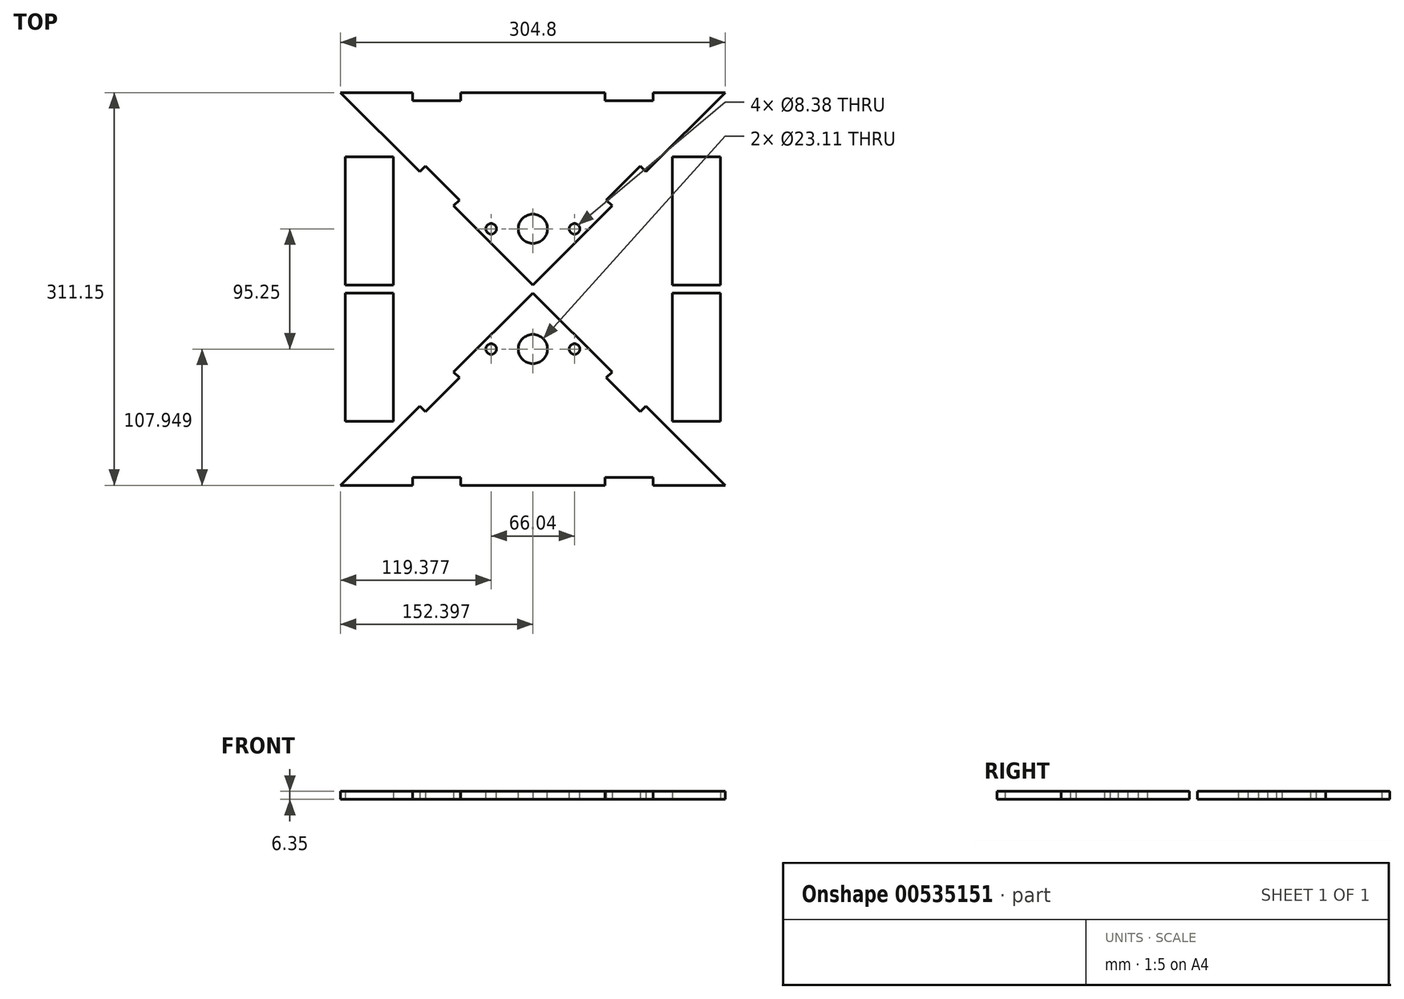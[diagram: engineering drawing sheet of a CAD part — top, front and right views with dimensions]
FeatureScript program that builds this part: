
annotation { "Feature Type Name" : "Feature", "Feature Type Description" : "" }
export const myFeature = defineFeature(function(context is Context, id is Id, definition is map)
    precondition{}
    {
        {
            var Q0;
            Q0=qCreatedBy(makeId("Top.planeOp"),FACE);
            var sketch = newSketch(context, id + "F0", { "sketchPlane" : qUnion([Q0])});
            skLineSegment(sketch, "E0", {"start": v(-161.55, -33.56) * mm, "end": v(143.25, -33.56) * mm});
            skLineSegment(sketch, "E1", {"start": v(143.25, -33.56) * mm, "end": v(-9.15, 118.84) * mm});
            skLineSegment(sketch, "E2", {"start": v(-9.15, 118.84) * mm, "end": v(-161.55, -33.56) * mm});
            skLineSegment(sketch, "E3", {"start": v(-213.92, 122.01) * mm, "end": v(339.98, 122.01) * mm, "construction": true});
            skSolve(sketch);
        }
        {
            var Q0;
            Q0=makeQuery(id+"F0.imprint","IMPRINT",FACE,{"disambiguationData":[TD([[makeQuery(id+"F0.imprint","IMPRINT",EDGE,{"derivedFrom":sQuery(id+"F0.wireOp",EDGE,"E0")}),1.0]])]});
            extrude(context, id + "F1", {"entities" : qUnion([Q0]), "depth" : 6.35 * mm});
        }
        {
            var Q0;
            Q0=makeQuery(id+"F1.opExtrude","CAP_FACE",FACE,{"disambiguationData":[OSD([sQuery(id+"F0.wireOp",EDGE,"E0"),sQuery(id+"F0.wireOp",EDGE,"E1"),sQuery(id+"F0.wireOp",EDGE,"E2")])],"isStart":false});
            var sketch = newSketch(context, id + "F2", { "sketchPlane" : qUnion([Q0])});
            skLineSegment(sketch, "E4", {"start": v(-9.15, 120.16) * mm, "end": v(-9.15, -59.52) * mm, "construction": true});
            skCircle(sketch, "E5", {"center": v(-9.15, 74.39) * mm, "radius": 11.56 * mm});
            skSolve(sketch);
        }
        {
            var Q0;
            Q0=makeQuery(id+"F2.imprint","IMPRINT",FACE,{"disambiguationData":[TD([[makeQuery(id+"F2.imprint","IMPRINT",EDGE,{"derivedFrom":sQuery(id+"F2.wireOp",EDGE,"E5")}),1.0]])]});
            extrude(context, id + "F3", {"entities" : qUnion([Q0]), "operationType" : NewBodyOperationType.REMOVE, "oppositeDirection" : true, "depth" : 25.4 * mm});
        }
        {
            var Q0;
            Q0=qCreatedBy(makeId("Top.planeOp"),FACE);
            var sketch = newSketch(context, id + "F4", { "sketchPlane" : qUnion([Q0])});
            skLineSegment(sketch, "E6.bottom", {"start": v(-157.83, 118.84) * mm, "end": v(-119.73, 118.84) * mm});
            skLineSegment(sketch, "E6.top", {"start": v(-157.83, 17.24) * mm, "end": v(-119.73, 17.24) * mm});
            skLineSegment(sketch, "E6.left", {"start": v(-157.83, 118.84) * mm, "end": v(-157.83, 17.24) * mm});
            skLineSegment(sketch, "E6.right", {"start": v(-119.73, 118.84) * mm, "end": v(-119.73, 17.24) * mm});
            skLineSegment(sketch, "E7.bottom", {"start": v(139.53, 118.84) * mm, "end": v(101.43, 118.84) * mm});
            skLineSegment(sketch, "E7.top", {"start": v(139.53, 17.24) * mm, "end": v(101.43, 17.24) * mm});
            skLineSegment(sketch, "E7.left", {"start": v(139.53, 118.84) * mm, "end": v(139.53, 17.24) * mm});
            skLineSegment(sketch, "E7.right", {"start": v(101.43, 118.84) * mm, "end": v(101.43, 17.24) * mm});
            skLineSegment(sketch, "E8.bottom", {"start": v(-157.83, 125.19) * mm, "end": v(-119.73, 125.19) * mm});
            skLineSegment(sketch, "E8.top", {"start": v(-157.83, 226.79) * mm, "end": v(-119.73, 226.79) * mm});
            skLineSegment(sketch, "E8.left", {"start": v(-157.83, 125.19) * mm, "end": v(-157.83, 226.79) * mm});
            skLineSegment(sketch, "E8.right", {"start": v(-119.73, 125.19) * mm, "end": v(-119.73, 226.79) * mm});
            skLineSegment(sketch, "E9.bottom", {"start": v(101.43, 125.19) * mm, "end": v(139.53, 125.19) * mm});
            skLineSegment(sketch, "E9.top", {"start": v(101.43, 226.79) * mm, "end": v(139.53, 226.79) * mm});
            skLineSegment(sketch, "E9.left", {"start": v(101.43, 125.19) * mm, "end": v(101.43, 226.79) * mm});
            skLineSegment(sketch, "E9.right", {"start": v(139.53, 125.19) * mm, "end": v(139.53, 226.79) * mm});
            skSolve(sketch);
        }
        {
            var Q0;
            Q0=makeQuery(id+"F1.opExtrude","SWEPT_FACE",FACE,{"disambiguationData":[OSD([sQuery(id+"F0.wireOp",EDGE,"E0")])]});
            cPlane(context, id + "F5", {"entities" : qUnion([Q0]), "cplaneType" : CPlaneType.OFFSET, "offset" : 155.57 * mm, "oppositeDirection" : true, "width" : 152.4 * mm, "height" : 152.4 * mm});
        }
        {
            var Q0;
            Q0=makeQuery(id+"F4.imprint","IMPRINT",FACE,{"disambiguationData":[TD([[makeQuery(id+"F4.imprint","IMPRINT",EDGE,{"derivedFrom":sQuery(id+"F4.wireOp",EDGE,"E8.bottom")}),1.0]])]});
            var Q1;
            Q1=makeQuery(id+"F4.imprint","IMPRINT",FACE,{"disambiguationData":[TD([[makeQuery(id+"F4.imprint","IMPRINT",EDGE,{"derivedFrom":sQuery(id+"F4.wireOp",EDGE,"E6.bottom")}),-1.0]])]});
            var Q2;
            Q2=makeQuery(id+"F4.imprint","IMPRINT",FACE,{"disambiguationData":[TD([[makeQuery(id+"F4.imprint","IMPRINT",EDGE,{"derivedFrom":sQuery(id+"F4.wireOp",EDGE,"E9.bottom")}),1.0]])]});
            var Q3;
            Q3=makeQuery(id+"F4.imprint","IMPRINT",FACE,{"disambiguationData":[TD([[makeQuery(id+"F4.imprint","IMPRINT",EDGE,{"derivedFrom":sQuery(id+"F4.wireOp",EDGE,"E7.bottom")}),1.0]])]});
            extrude(context, id + "F6", {"entities" : qUnion([Q0, Q1, Q2, Q3]), "depth" : 6.35 * mm});
        }
        {
            var Q0;
            Q0=qCreatedBy(makeId("Top.planeOp"),FACE);
            var sketch = newSketch(context, id + "F7", { "sketchPlane" : qUnion([Q0])});
            skLineSegment(sketch, "E10.bottom", {"start": v(-104.4, -33.56) * mm, "end": v(-66.3, -33.56) * mm});
            skLineSegment(sketch, "E10.top", {"start": v(-104.4, -27.21) * mm, "end": v(-66.3, -27.21) * mm});
            skLineSegment(sketch, "E10.left", {"start": v(-104.4, -33.56) * mm, "end": v(-104.4, -27.21) * mm});
            skLineSegment(sketch, "E10.right", {"start": v(-66.3, -33.56) * mm, "end": v(-66.3, -27.21) * mm});
            skLineSegment(sketch, "E11.bottom", {"start": v(48, -33.56) * mm, "end": v(86.1, -33.56) * mm});
            skLineSegment(sketch, "E11.top", {"start": v(48, -27.21) * mm, "end": v(86.1, -27.21) * mm});
            skLineSegment(sketch, "E11.left", {"start": v(48, -33.56) * mm, "end": v(48, -27.21) * mm});
            skLineSegment(sketch, "E11.right", {"start": v(86.1, -33.56) * mm, "end": v(86.1, -27.21) * mm});
            skLineSegment(sketch, "E12", {"start": v(80.52, 29.17) * mm, "end": v(53.58, 56.1) * mm});
            skLineSegment(sketch, "E13", {"start": v(53.58, 56.1) * mm, "end": v(49.09, 51.62) * mm});
            skLineSegment(sketch, "E14", {"start": v(49.09, 51.62) * mm, "end": v(76.03, 24.68) * mm});
            skLineSegment(sketch, "E15", {"start": v(76.03, 24.68) * mm, "end": v(80.52, 29.17) * mm});
            skLineSegment(sketch, "E16", {"start": v(-98.82, 29.17) * mm, "end": v(-71.88, 56.1) * mm});
            skLineSegment(sketch, "E17", {"start": v(-71.88, 56.1) * mm, "end": v(-67.4, 51.62) * mm});
            skLineSegment(sketch, "E18", {"start": v(-67.4, 51.62) * mm, "end": v(-94.33, 24.68) * mm});
            skLineSegment(sketch, "E19", {"start": v(-94.33, 24.68) * mm, "end": v(-98.82, 29.17) * mm});
            skLineSegment(sketch, "E20", {"start": v(93.42, 69) * mm, "end": v(-21.4, -45.81) * mm, "construction": true});
            skLineSegment(sketch, "E21", {"start": v(-105.13, 62.41) * mm, "end": v(39.8, -82.5) * mm, "construction": true});
            skLineSegment(sketch, "E22", {"start": v(-294.6, 122.01) * mm, "end": v(243.28, 122.01) * mm, "construction": true});
            skLineSegment(sketch, "E23", {"start": v(-9.15, 388.68) * mm, "end": v(-9.15, -215.92) * mm, "construction": true});
            skSolve(sketch);
        }
        {
            var Q0;
            Q0=makeQuery(id+"F7.imprint","IMPRINT",FACE,{"disambiguationData":[TD([[makeQuery(id+"F7.imprint","IMPRINT",EDGE,{"derivedFrom":sQuery(id+"F7.wireOp",EDGE,"E12")}),1.0]])]});
            var Q1;
            Q1=makeQuery(id+"F7.imprint","IMPRINT",FACE,{"disambiguationData":[TD([[makeQuery(id+"F7.imprint","IMPRINT",EDGE,{"derivedFrom":sQuery(id+"F7.wireOp",EDGE,"E16")}),-1.0]])]});
            var Q2;
            Q2=makeQuery(id+"F7.imprint","IMPRINT",FACE,{"disambiguationData":[TD([[makeQuery(id+"F7.imprint","IMPRINT",EDGE,{"derivedFrom":sQuery(id+"F7.wireOp",EDGE,"E10.bottom")}),1.0]])]});
            var Q3;
            Q3=makeQuery(id+"F7.imprint","IMPRINT",FACE,{"disambiguationData":[TD([[makeQuery(id+"F7.imprint","IMPRINT",EDGE,{"derivedFrom":sQuery(id+"F7.wireOp",EDGE,"E11.bottom")}),1.0]])]});
            extrude(context, id + "F8", {"entities" : qUnion([Q0, Q1, Q2, Q3]), "operationType" : NewBodyOperationType.REMOVE, "depth" : 25.4 * mm});
        }
        {
            var Q0;
            Q0=makeQuery(id+"F1.opExtrude","CAP_FACE",FACE,{"disambiguationData":[OSD([sQuery(id+"F0.wireOp",EDGE,"E0"),sQuery(id+"F0.wireOp",EDGE,"E1"),sQuery(id+"F0.wireOp",EDGE,"E2")])],"isStart":false});
            var sketch = newSketch(context, id + "F9", { "sketchPlane" : qUnion([Q0])});
            skLineSegment(sketch, "E24", {"start": v(-214.23, 74.39) * mm, "end": v(252.42, 74.39) * mm, "construction": true});
            skLineSegment(sketch, "E25", {"start": v(-9.15, 305.95) * mm, "end": v(-9.15, -55.57) * mm, "construction": true});
            skCircle(sketch, "E26", {"center": v(23.87, 74.39) * mm, "radius": 4.2 * mm});
            skCircle(sketch, "E27", {"center": v(-42.17, 74.39) * mm, "radius": 4.2 * mm});
            skSolve(sketch);
        }
        {
            var Q0;
            Q0=makeQuery(id+"F9.imprint","IMPRINT",FACE,{"disambiguationData":[TD([[makeQuery(id+"F9.imprint","IMPRINT",EDGE,{"derivedFrom":sQuery(id+"F9.wireOp",EDGE,"E27")}),1.0]])]});
            var Q1;
            Q1=makeQuery(id+"F9.imprint","IMPRINT",FACE,{"disambiguationData":[TD([[makeQuery(id+"F9.imprint","IMPRINT",EDGE,{"derivedFrom":sQuery(id+"F9.wireOp",EDGE,"E26")}),1.0]])]});
            extrude(context, id + "F10", {"entities" : qUnion([Q0, Q1]), "operationType" : NewBodyOperationType.REMOVE, "oppositeDirection" : true, "depth" : 25.4 * mm});
        }
        {
            var Q0;
            Q0=makeQuery(id+"F1.opExtrude","SWEPT_BODY",BODY,{"disambiguationData":[OSD([sQuery(id+"F0.wireOp",EDGE,"E0"),sQuery(id+"F0.wireOp",EDGE,"E1"),sQuery(id+"F0.wireOp",EDGE,"E2")])]});
            var Q1;
            Q1=qCreatedBy(id+"F5.planeOp",FACE);
            mirror(context, id + "F11", {"entities" : qUnion([Q0]), "mirrorPlane" : qUnion([Q1])});
        }
    });
